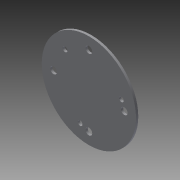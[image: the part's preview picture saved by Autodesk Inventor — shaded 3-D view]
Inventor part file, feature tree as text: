
AUTODESK INVENTOR PART (.ipt)
format: ipt  version: 2015 (Build 190159000, 159)  size: 111,104 bytes
history: native  units: mm
features: extrude x3, other x1, sketch x1
ambient origin geometry x8: Origin, YZ Plane, XZ Plane, XY Plane, X Axis, Y Axis, Z Axis, Center Point
bodies: Body1 (feature_tree)
feature tree (5):
  other  "ソリッド1"
  sketch  "スケッチ1"
  extrude  "押し出し1"  Depth=100.0mm
  extrude  "押し出し2"  Depth=63.0mm
  extrude  "押し出し3"  Depth=6.0mm
